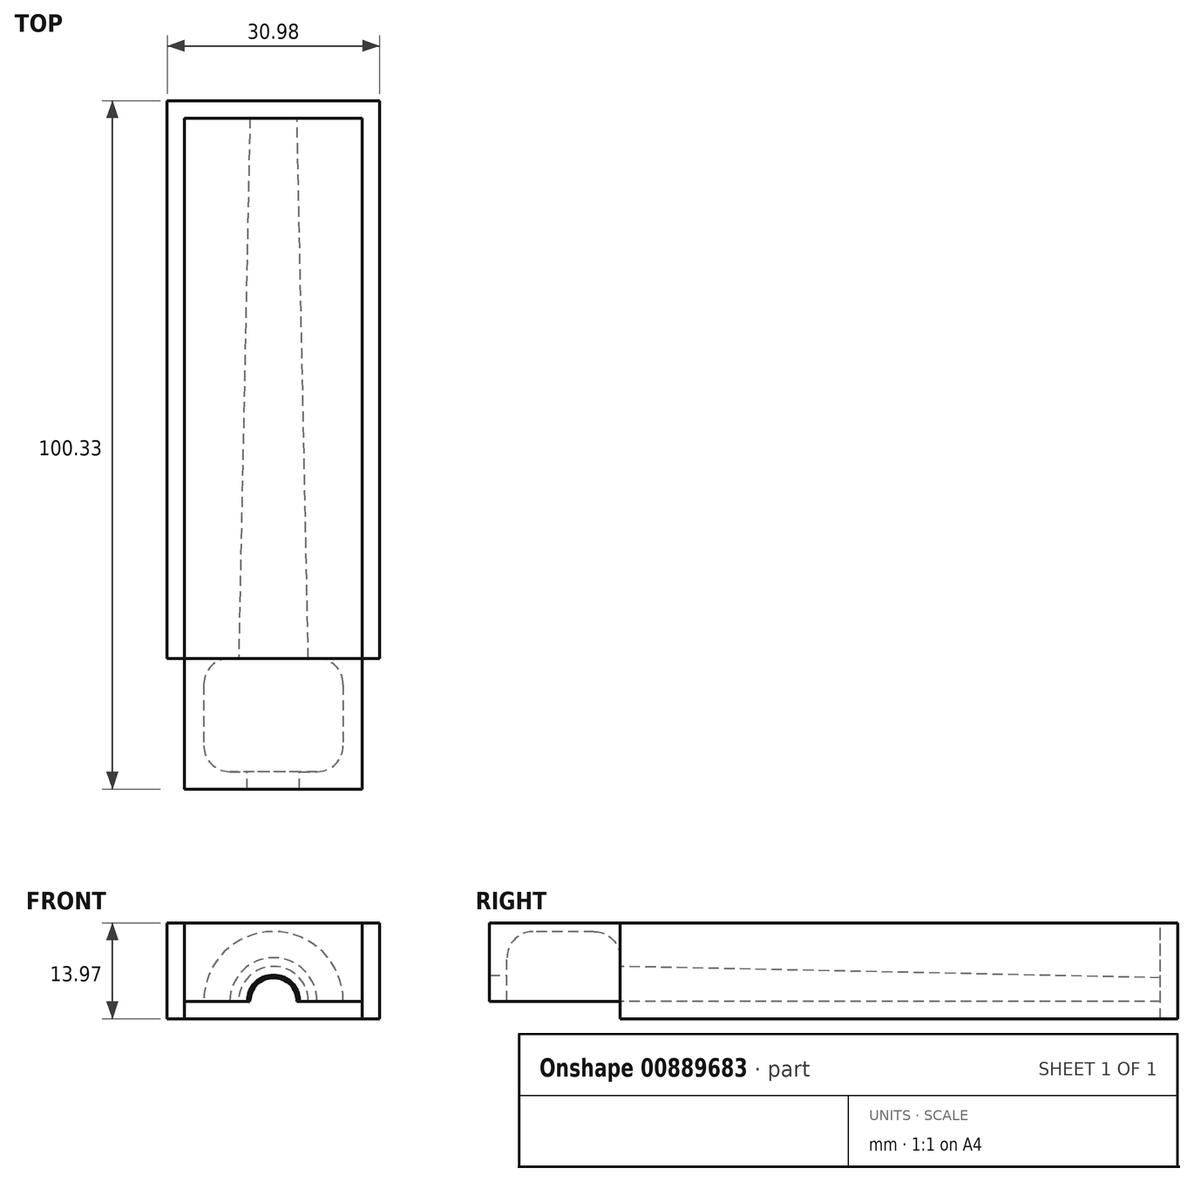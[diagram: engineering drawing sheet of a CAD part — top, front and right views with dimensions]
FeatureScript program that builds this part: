
annotation { "Feature Type Name" : "Feature", "Feature Type Description" : "" }
export const myFeature = defineFeature(function(context is Context, id is Id, definition is map)
    precondition{}
    {
        {
            var Q0;
            Q0=qCreatedBy(makeId("Top.planeOp"),FACE);
            var sketch = newSketch(context, id + "F0", { "sketchPlane" : qUnion([Q0])});
            skLineSegment(sketch, "E0", {"start": v(26.74, -13.67) * mm, "end": v(26.74, -13.67) * mm});
            skLineSegment(sketch, "E1.bottom", {"start": v(12.95, -39.37) * mm, "end": v(-12.95, -39.37) * mm});
            skLineSegment(sketch, "E1.top", {"start": v(12.95, 39.37) * mm, "end": v(-12.95, 39.37) * mm});
            skLineSegment(sketch, "E1.left", {"start": v(12.95, -39.37) * mm, "end": v(12.95, 39.37) * mm});
            skLineSegment(sketch, "E1.right", {"start": v(-12.95, -39.37) * mm, "end": v(-12.95, 39.37) * mm});
            skPoint(sketch, "E1.middle", {"position": v(0, 0) * mm});
            skSolve(sketch);
        }
        {
            var Q0;
            Q0 = qSketchRegion(id + "F0", true);
            extrude(context, id + "F1", {"entities" : qUnion([Q0]), "oppositeDirection" : true, "depth" : 11.43 * mm, "offsetDistance" : 25.4 * mm});
        }
        {
            var Q0;
            Q0=qCreatedBy(makeId("Top.planeOp"),FACE);
            var sketch = newSketch(context, id + "F2", { "sketchPlane" : qUnion([Q0])});
            skPoint(sketch, "E2", {"position": v(0, 0) * mm});
            skLineSegment(sketch, "E3", {"start": v(-15.5, 41.91) * mm, "end": v(15.5, 41.91) * mm});
            skLineSegment(sketch, "E4", {"start": v(15.5, 41.91) * mm, "end": v(15.5, -39.37) * mm});
            skLineSegment(sketch, "E5", {"start": v(15.5, -39.37) * mm, "end": v(-15.5, -39.37) * mm});
            skLineSegment(sketch, "E6", {"start": v(-15.5, -39.37) * mm, "end": v(-15.5, 41.91) * mm});
            skLineSegment(sketch, "E7.left", {"start": v(27.03, -11.85) * mm, "end": v(27.03, -11.85) * mm});
            skLineSegment(sketch, "E7.right", {"start": v(28.6, -11.85) * mm, "end": v(28.6, -11.85) * mm});
            skLineSegment(sketch, "E8", {"start": v(-12.95, -39.37) * mm, "end": v(-12.95, 39.37) * mm});
            skLineSegment(sketch, "E9", {"start": v(-12.95, 39.37) * mm, "end": v(12.95, 39.37) * mm});
            skLineSegment(sketch, "E10", {"start": v(12.95, 39.37) * mm, "end": v(12.95, -39.37) * mm});
            skSolve(sketch);
        }
        {
            var Q0;
            Q0=makeQuery(id+"F2.imprint","IMPRINT",FACE,{"disambiguationData":[TD([[makeQuery(id+"F2.imprint","IMPRINT",EDGE,{"derivedFrom":sQuery(id+"F2.wireOp",EDGE,"E3")}),-1.0]])]});
            extrude(context, id + "F3", {"entities" : qUnion([Q0]), "oppositeDirection" : true, "depth" : 13.97 * mm, "offsetDistance" : 25.4 * mm});
        }
        {
            var Q0;
            Q0=makeQuery(id+"F1.opExtrude","CAP_FACE",FACE,{"disambiguationData":[OSD([sQuery(id+"F0.wireOp",EDGE,"E1.bottom"),sQuery(id+"F0.wireOp",EDGE,"E1.top"),sQuery(id+"F0.wireOp",EDGE,"E1.left"),sQuery(id+"F0.wireOp",EDGE,"E1.right")])],"isStart":false});
            var sketch = newSketch(context, id + "F4", { "sketchPlane" : qUnion([Q0])});
            skLineSegment(sketch, "E11", {"start": v(5.08, 39.37) * mm, "end": v(3.43, -39.37) * mm});
            skLineSegment(sketch, "E12", {"start": v(3.43, -39.37) * mm, "end": v(0, -39.37) * mm});
            skLineSegment(sketch, "E13", {"start": v(0, -39.37) * mm, "end": v(0, 39.37) * mm});
            skLineSegment(sketch, "E14", {"start": v(0, 39.37) * mm, "end": v(5.08, 39.37) * mm});
            skSolve(sketch);
        }
        {
            var Q0;
            Q0=makeQuery(id+"F4.imprint","IMPRINT",FACE,{"disambiguationData":[TD([[makeQuery(id+"F4.imprint","IMPRINT",EDGE,{"derivedFrom":sQuery(id+"F4.wireOp",EDGE,"E11")}),-1.0]])]});
            var Q1;
            Q1=sQuery(id+"F4.wireOp",EDGE,"E13");
            revolve(context, id + "F5", {"operationType" : NewBodyOperationType.REMOVE, "surfaceOperationType" : NewSurfaceOperationType.NEW, "entities" : qUnion([Q0]), "axis" : qUnion([Q1]), "revolveType" : RevolveType.FULL, "oppositeDirection" : true});
        }
        {
            var Q0;
            Q0=qCreatedBy(makeId("Top.planeOp"),FACE);
            var sketch = newSketch(context, id + "F6", { "sketchPlane" : qUnion([Q0])});
            skLineSegment(sketch, "E15.right", {"start": v(12.95, -55.88) * mm, "end": v(12.95, -39.37) * mm});
            skLineSegment(sketch, "E16", {"start": v(0, -55.88) * mm, "end": v(0, -39.37) * mm});
            skLineSegment(sketch, "E17", {"start": v(-12.95, -39.37) * mm, "end": v(12.95, -39.37) * mm});
            skLineSegment(sketch, "E18", {"start": v(-12.95, -55.88) * mm, "end": v(12.95, -55.88) * mm});
            skLineSegment(sketch, "E19", {"start": v(-12.95, -39.37) * mm, "end": v(-12.95, -55.88) * mm});
            skSolve(sketch);
        }
        {
            var Q0;
            {var subQ0=sQuery(id+"F6.wireOp",EDGE,"E15.right");Q0=makeQuery(id+"F6.imprint","IMPRINT",FACE,{"disambiguationData":[TD([[makeQuery(id+"F6.imprint","IMPRINT",EDGE,{"derivedFrom":subQ0}),1.0]])]});}
            var Q1;
            {var subQ0=sQuery(id+"F6.wireOp",EDGE,"E16");Q1=makeQuery(id+"F6.imprint","IMPRINT",FACE,{"disambiguationData":[TD([[makeQuery(id+"F6.imprint","IMPRINT",EDGE,{"derivedFrom":subQ0}),1.0]])]});}
            extrude(context, id + "F7", {"entities" : qUnion([Q0, Q1]), "oppositeDirection" : true, "depth" : 11.43 * mm, "offsetDistance" : 25.4 * mm});
        }
        {
            var Q0;
            Q0=makeQuery(id+"F7.opExtrude","CAP_FACE",FACE,{"disambiguationData":[OSD([sQuery(id+"F6.wireOp",EDGE,"E15.bottom"),sQuery(id+"F6.wireOp",EDGE,"E15.left"),sQuery(id+"F6.wireOp",EDGE,"E15.right"),sQuery(id+"F6.wireOp",EDGE,"efe82397-11cd-47b6-ac99-3fd2d8ea4329"),sQuery(id+"F6.wireOp",EDGE,"E17")])],"isStart":false});
            var sketch = newSketch(context, id + "F8", { "sketchPlane" : qUnion([Q0])});
            skLineSegment(sketch, "E20", {"start": v(6.35, 55.88) * mm, "end": v(6.35, 55.88) * mm});
            skLineSegment(sketch, "E21", {"start": v(0, 55.88) * mm, "end": v(6.35, 55.88) * mm});
            skLineSegment(sketch, "E22", {"start": v(10.16, 52.07) * mm, "end": v(10.16, 43.18) * mm});
            skLineSegment(sketch, "E23", {"start": v(6.35, 39.37) * mm, "end": v(0, 39.37) * mm});
            skLineSegment(sketch, "E24", {"start": v(0, 39.37) * mm, "end": v(0, 55.88) * mm});
            skPoint(sketch, "E25.visualSharp", {"position": v(10.16, 55.88) * mm});
            skArc(sketch, "E25.filletArc", {"start": v(10.16, 52.07) * mm, "mid": v(9.04, 54.76) * mm, "end": v(6.35, 55.88) * mm});
            skPoint(sketch, "E26.visualSharp", {"position": v(10.16, 39.37) * mm});
            skArc(sketch, "E26.filletArc", {"start": v(6.35, 39.37) * mm, "mid": v(9.04, 40.49) * mm, "end": v(10.16, 43.18) * mm});
            skSolve(sketch);
        }
        {
            var Q0;
            Q0=makeQuery(id+"F8.imprint","IMPRINT",FACE,{"disambiguationData":[TD([[makeQuery(id+"F8.imprint","IMPRINT",EDGE,{"derivedFrom":sQuery(id+"F8.wireOp",EDGE,"E21")}),-1.0]])]});
            var Q1;
            Q1=sQuery(id+"F8.wireOp",EDGE,"E24");
            revolve(context, id + "F9", {"operationType" : NewBodyOperationType.REMOVE, "surfaceOperationType" : NewSurfaceOperationType.NEW, "entities" : qUnion([Q0]), "axis" : qUnion([Q1]), "revolveType" : RevolveType.FULL, "oppositeDirection" : true});
        }
        {
            var Q0;
            Q0=makeQuery(id+"F7.opExtrude","SWEPT_FACE",FACE,{"disambiguationData":[OSD([sQuery(id+"F6.wireOp",EDGE,"E18")])]});
            var sketch = newSketch(context, id + "F10", { "sketchPlane" : qUnion([Q0])});
            skLineSegment(sketch, "E27.bottom", {"start": v(-12.95, 0) * mm, "end": v(12.95, 0) * mm});
            skLineSegment(sketch, "E27.top", {"start": v(-12.95, -11.43) * mm, "end": v(12.95, -11.43) * mm});
            skLineSegment(sketch, "E27.left", {"start": v(-12.95, 0) * mm, "end": v(-12.95, -11.43) * mm});
            skLineSegment(sketch, "E27.right", {"start": v(12.95, 0) * mm, "end": v(12.95, -11.43) * mm});
            skArc(sketch, "E28", {"start": v(3.8, -11.43) * mm, "mid": v(0, -7.62) * mm, "end": v(-3.81, -11.43) * mm});
            skSolve(sketch);
        }
        {
            var Q0;
            Q0=makeQuery(id+"F10.imprint","IMPRINT",FACE,{"disambiguationData":[TD([[makeQuery(id+"F10.imprint","IMPRINT",EDGE,{"derivedFrom":sQuery(id+"F10.wireOp",EDGE,"E27.bottom")}),-1.0]])]});
            var Q1;
            {var subQ2=sQuery(id+"F10.wireOp",EDGE,"E28");Q1=makeQuery(id+"F10.imprint","IMPRINT",FACE,{"disambiguationData":[TD([[makeQuery(id+"F10.imprint","IMPRINT",EDGE,{"derivedFrom":subQ2}),-1.0]])]});}
            extrude(context, id + "F11", {"entities" : qUnion([Q0, Q1]), "operationType" : NewBodyOperationType.ADD, "depth" : 2.54 * mm, "offsetDistance" : 25.4 * mm});
        }
    });
